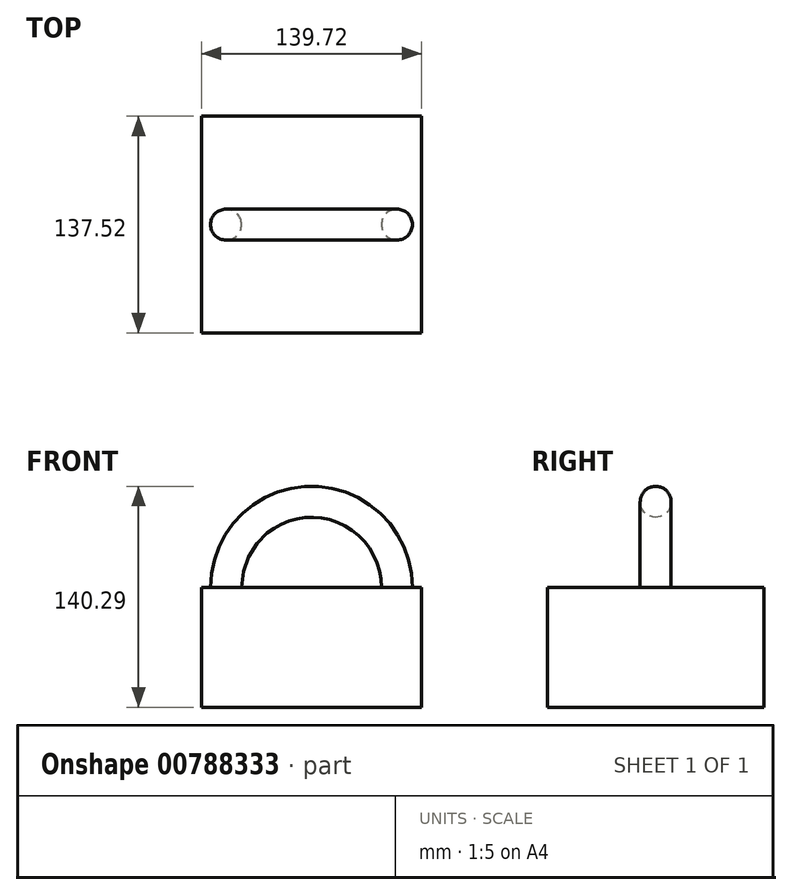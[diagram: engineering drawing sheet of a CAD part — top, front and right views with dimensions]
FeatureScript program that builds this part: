
annotation { "Feature Type Name" : "Feature", "Feature Type Description" : "" }
export const myFeature = defineFeature(function(context is Context, id is Id, definition is map)
    precondition{}
    {
        {
            var Q0;
            Q0=qCreatedBy(makeId("Top.planeOp"),FACE);
            var sketch = newSketch(context, id + "F0", { "sketchPlane" : qUnion([Q0])});
            skLineSegment(sketch, "E0.bottom", {"start": v(69.86, -68.76) * mm, "end": v(-69.86, -68.76) * mm});
            skLineSegment(sketch, "E0.top", {"start": v(69.86, 68.76) * mm, "end": v(-69.86, 68.76) * mm});
            skLineSegment(sketch, "E0.left", {"start": v(69.86, -68.76) * mm, "end": v(69.86, 68.76) * mm});
            skLineSegment(sketch, "E0.right", {"start": v(-69.86, -68.76) * mm, "end": v(-69.86, 68.76) * mm});
            skPoint(sketch, "E0.middle", {"position": v(0, 0) * mm});
            skLineSegment(sketch, "E1", {"start": v(0, 68.76) * mm, "end": v(0, -68.76) * mm});
            skSolve(sketch);
        }
        {
            var Q0;
            Q0=qCreatedBy(makeId("Top.planeOp"),FACE);
            var sketch = newSketch(context, id + "F1", { "sketchPlane" : qUnion([Q0])});
            skCircle(sketch, "E2", {"center": v(54.26, 0) * mm, "radius": 9.82 * mm});
            skSolve(sketch);
        }
        {
            var Q0;
            {var subQ0=sQuery(id+"F0.wireOp",EDGE,"E0.left");Q0=makeQuery(id+"F0.imprint","IMPRINT",FACE,{"disambiguationData":[TD([[makeQuery(id+"F0.imprint","IMPRINT",EDGE,{"derivedFrom":subQ0}),1.0]])]});}
            var Q1;
            {var subQ0=sQuery(id+"F0.wireOp",EDGE,"E0.right");Q1=makeQuery(id+"F0.imprint","IMPRINT",FACE,{"disambiguationData":[TD([[makeQuery(id+"F0.imprint","IMPRINT",EDGE,{"derivedFrom":subQ0}),-1.0]])]});}
            extrude(context, id + "F2", {"entities" : qUnion([Q0, Q1]), "depth" : -76.2 * mm, "offsetDistance" : 25.4 * mm});
        }
        {
            var Q0;
            Q0 = qSketchRegion(id + "F1", true);
            var Q1;
            Q1=sQuery(id+"F0.wireOp",EDGE,"E1");
            revolve(context, id + "F3", {"operationType" : NewBodyOperationType.ADD, "surfaceOperationType" : NewSurfaceOperationType.NEW, "entities" : qUnion([Q0]), "axis" : qUnion([Q1]), "revolveType" : RevolveType.FULL});
        }
    });
